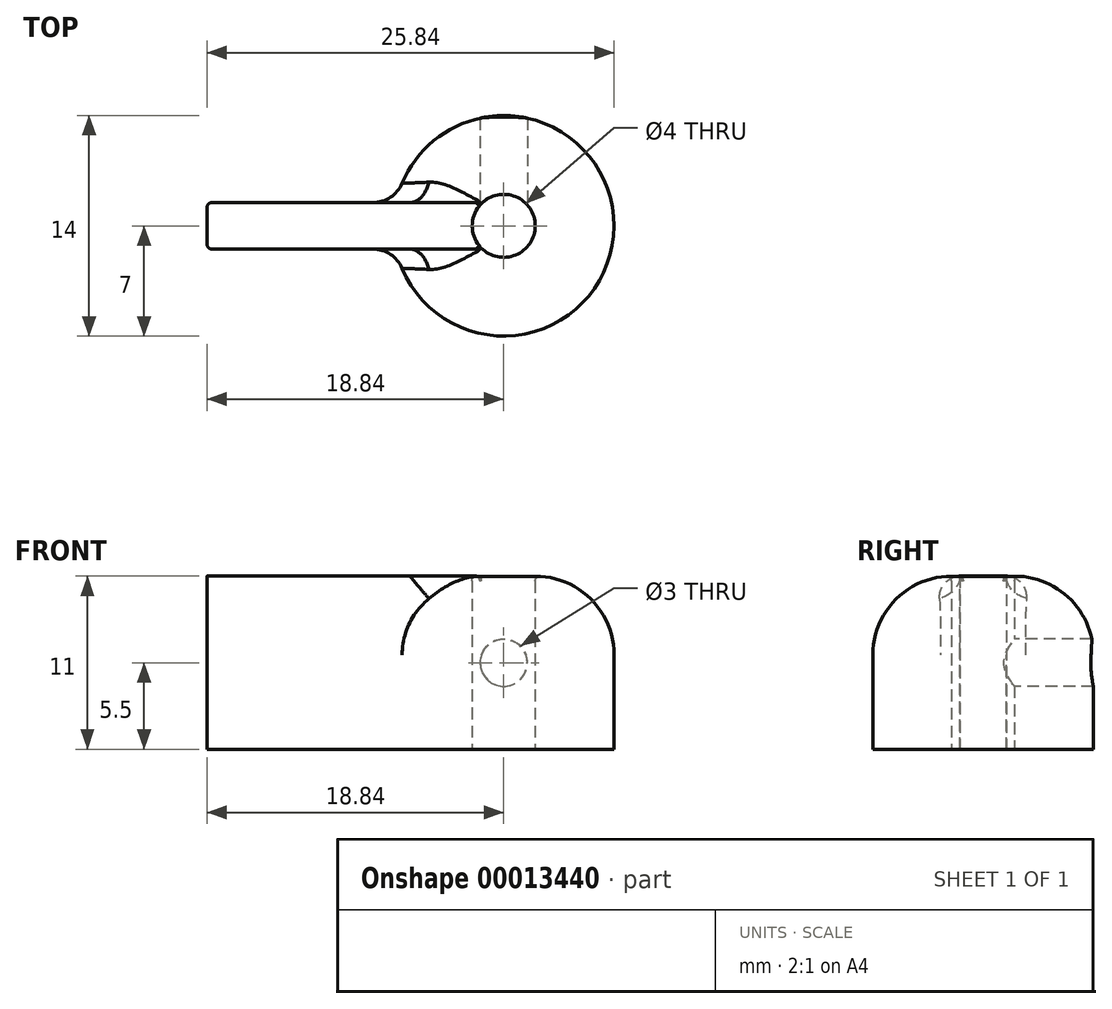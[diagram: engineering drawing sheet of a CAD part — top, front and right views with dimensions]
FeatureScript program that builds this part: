
annotation { "Feature Type Name" : "Feature", "Feature Type Description" : "" }
export const myFeature = defineFeature(function(context is Context, id is Id, definition is map)
    precondition{}
    {
        {
            var Q0;
            Q0=qCreatedBy(makeId("Top.planeOp"),FACE);
            var sketch = newSketch(context, id + "F0", { "sketchPlane" : qUnion([Q0])});
            skCircle(sketch, "E0", {"center": v(0, 0) * mm, "radius": 2 * mm});
            skCircle(sketch, "E1.0", {"center": v(0, 0) * mm, "radius": 7 * mm});
            skLineSegment(sketch, "E2", {"start": v(-6.84, 1.48) * mm, "end": v(-18.84, 1.48) * mm});
            skLineSegment(sketch, "E3", {"start": v(-18.84, 1.48) * mm, "end": v(-18.84, -1.48) * mm});
            skLineSegment(sketch, "E4", {"start": v(-18.84, -1.48) * mm, "end": v(-6.84, -1.48) * mm});
            skSolve(sketch);
        }
        {
            var Q0;
            Q0 = qSketchRegion(id + "F0", true);
            extrude(context, id + "F1", {"entities" : qUnion([Q0]), "depth" : 11 * mm});
        }
        {
            var Q0;
            Q0=qCreatedBy(makeId("Front.planeOp"),FACE);
            var sketch = newSketch(context, id + "F2", { "sketchPlane" : qUnion([Q0])});
            skCircle(sketch, "E5", {"center": v(0, 5.5) * mm, "radius": 1.5 * mm});
            skSolve(sketch);
        }
        {
            var Q0;
            Q0 = qSketchRegion(id + "F2", true);
            extrude(context, id + "F3", {"entities" : qUnion([Q0]), "operationType" : NewBodyOperationType.REMOVE, "endBound" : BoundingType.THROUGH_ALL, "oppositeDirection" : true, "depth" : 25 * mm});
        }
        {
            var Q0;
            Q0=makeQuery(id+"F1.opExtrude","CAP_EDGE",EDGE,{"disambiguationData":[OSD([sQuery(id+"F0.wireOp",EDGE,"E1.0")])],"isStart":false});
            fillet(context, id + "F4", {"entities" : qUnion([Q0]), "radius" : 5 * mm, "tangentPropagation" : true, "allowEdgeOverflow" : false});
        }
        {
            var Q0;
            Q0=makeQuery(id+"F1.opExtrude","SWEPT_EDGE",EDGE,{"disambiguationData":[OSD([sQuery(id+"F0.wireOp",EDGE,"E1.0"),sQuery(id+"F0.wireOp",EDGE,"E2")])]});
            var Q1;
            Q1=makeQuery(id+"F1.opExtrude","SWEPT_EDGE",EDGE,{"disambiguationData":[OSD([sQuery(id+"F0.wireOp",EDGE,"E1.0"),sQuery(id+"F0.wireOp",EDGE,"E4")])]});
            fillet(context, id + "F5", {"entities" : qUnion([Q0, Q1]), "radius" : 2 * mm, "tangentPropagation" : true, "allowEdgeOverflow" : false});
        }
        {
            var Q0;
            Q0=makeQuery(id+"F1.opExtrude","CAP_EDGE",EDGE,{"disambiguationData":[OSD([sQuery(id+"F0.wireOp",EDGE,"E0")])],"isStart":false});
            var Q1;
            Q1=makeQuery(id+"F4.opFillet","BLEND_EDGE",EDGE,{"blendedFrom":[makeQuery(id+"F1.opExtrude","CAP_EDGE",EDGE,{"disambiguationData":[OSD([sQuery(id+"F0.wireOp",EDGE,"E1.0")])],"isStart":false}),makeQuery(id+"F1.opExtrude","SWEPT_FACE",FACE,{"disambiguationData":[OSD([sQuery(id+"F0.wireOp",EDGE,"E0")])]})],"blendedInto":[makeQuery(id+"F1.opExtrude","SWEPT_FACE",FACE,{"disambiguationData":[OSD([sQuery(id+"F0.wireOp",EDGE,"E0")])]})]});
            var Q2;
            Q2=makeQuery(id+"F1.opExtrude","SWEPT_EDGE",EDGE,{"disambiguationData":[OSD([sQuery(id+"F0.wireOp",EDGE,"E2"),sQuery(id+"F0.wireOp",EDGE,"E3")])]});
            var Q3;
            Q3=makeQuery(id+"F1.opExtrude","SWEPT_EDGE",EDGE,{"disambiguationData":[OSD([sQuery(id+"F0.wireOp",EDGE,"E3"),sQuery(id+"F0.wireOp",EDGE,"E4")])]});
            fillet(context, id + "F6", {"entities" : qUnion([Q0, Q1, Q2, Q3]), "radius" : 0.3 * mm, "tangentPropagation" : true, "allowEdgeOverflow" : false});
        }
    });
